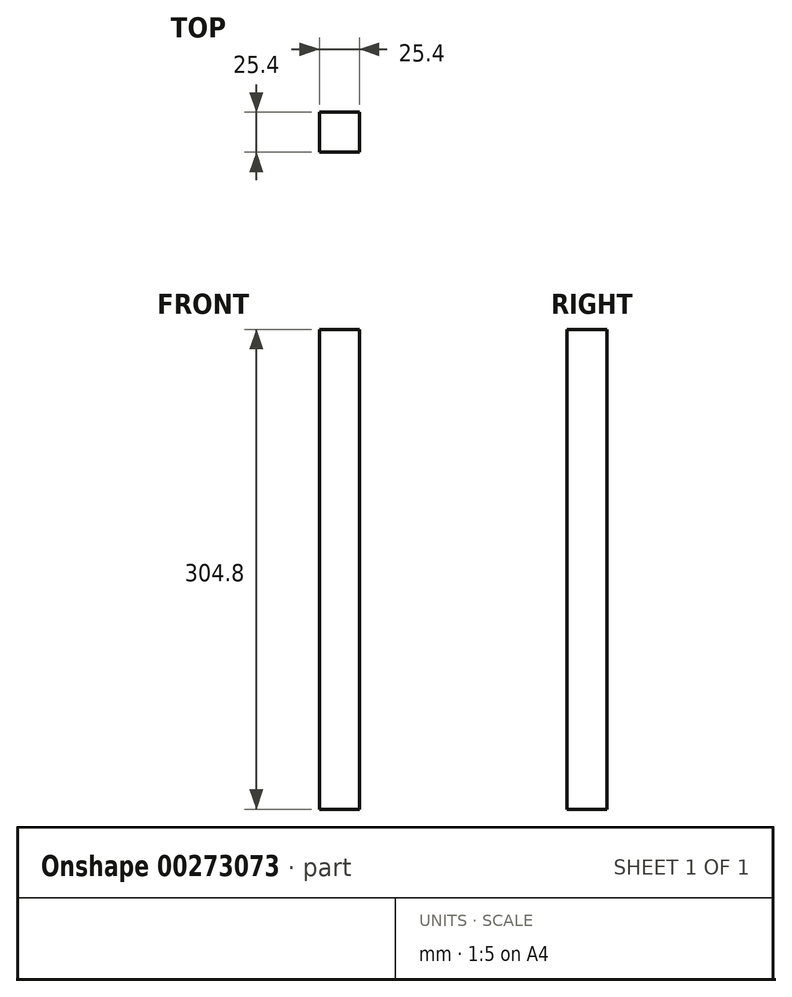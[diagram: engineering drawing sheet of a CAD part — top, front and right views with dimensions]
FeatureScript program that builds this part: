
annotation { "Feature Type Name" : "Feature", "Feature Type Description" : "" }
export const myFeature = defineFeature(function(context is Context, id is Id, definition is map)
    precondition{}
    {
        {
            var Q0;
            Q0=qCreatedBy(makeId("Front.planeOp"),FACE);
            var sketch = newSketch(context, id + "F0", { "sketchPlane" : qUnion([Q0])});
            skLineSegment(sketch, "E0.bottom", {"start": v(-48.87, 149.82) * mm, "end": v(-23.47, 149.82) * mm});
            skLineSegment(sketch, "E0.top", {"start": v(-48.87, -154.98) * mm, "end": v(-23.47, -154.98) * mm});
            skLineSegment(sketch, "E0.left", {"start": v(-48.87, 149.82) * mm, "end": v(-48.87, -154.98) * mm});
            skLineSegment(sketch, "E0.right", {"start": v(-23.47, 149.82) * mm, "end": v(-23.47, -154.98) * mm});
            skSolve(sketch);
        }
        {
            var Q0;
            Q0 = qSketchRegion(id + "F0", true);
            extrude(context, id + "F1", {"entities" : qUnion([Q0]), "depth" : 25.4 * mm});
        }
    });
